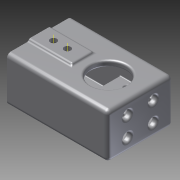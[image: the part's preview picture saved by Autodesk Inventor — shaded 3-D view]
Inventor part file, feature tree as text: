
AUTODESK INVENTOR PART (.ipt)
format: ipt  version: 2012 (Build 160160000, 160)  size: 1,043,968 bytes
history: native  units: mm
features: extrude x30, sketch x30, fillet x15, reference x11, projected_geometry x11, other x4
ambient origin geometry x8: Origin, YZ Plane, XZ Plane, XY Plane, X Axis, Y Axis, Z Axis, Center Point
bodies: Solid1 (feature_tree)
feature tree (101):
  extrude  "Extrusion1"  Depth=2.0mm
  extrude  "Extrusion2"  Depth=2.0mm
  extrude  "Extrusion4"  Depth=3.0mm
  extrude  "Extrusion5"  Depth=3.0mm
  extrude  "Extrusion6"  Depth=0.3mm
  extrude  "Extrusion7"  Depth=0.3mm
  fillet  "Fillet1"  Radius=0.7mm
  extrude  "Extrusion8"  Depth=3.0mm
  extrude  "Extrusion9"  Depth=3.0mm
  extrude  "Extrusion10"  Depth=2.3mm TaperAngle=0.0deg
  extrude  "Extrusion11"  Depth=0.7mm TaperAngle=0.0deg
  other  "Work Axis1"
  extrude  "Extrusion12"  Depth=0.5mm
  extrude  "Extrusion13"  Depth=20.0mm TaperAngle=0.0deg
  extrude  "Extrusion15"  Depth=0.3mm
  other  "Work Axis3"
  extrude  "Extrusion16"  Depth=4.0mm
  extrude  "Extrusion17"  Depth=1.0mm TaperAngle=0.0deg
  extrude  "Extrusion18"  Depth=10.0mm TaperAngle=0.0deg
  extrude  "Extrusion19"  Depth=10.0mm TaperAngle=0.0deg
  extrude  "Extrusion20"  Depth=10.0mm TaperAngle=0.0deg
  fillet  "Fillet3"  Radius=25.903503mm
  fillet  "Fillet4"  Radius=12.951751mm
  fillet  "Fillet5"  Radius=5.0mm
  extrude  "Extrusion21"  Depth=31.903503mm
  extrude  "Extrusion22"  Depth=10.6mm
  extrude  "Extrusion23"  Depth=3.3mm
  extrude  "Extrusion24"  Depth=5.509188mm
  fillet  "Fillet10"  Radius=1.695406mm
  extrude  "Extrusion25"  Depth=1.695406mm
  extrude  "Extrusion26"  Depth=0.6mm TaperAngle=0.0deg
  extrude  "Extrusion27"  Depth=2.0mm
  fillet  "Fillet12"  Radius=3.333333mm
  fillet  "Fillet13"  Radius=10.0mm
  fillet  "Fillet17"  Radius=20.0mm
  extrude  "Extrusion28"  Depth=1.25mm
  fillet  "Fillet18"  Radius=2.5mm
  extrude  "Extrusion29"  Depth=19.403503mm
  fillet  "Fillet19"  Radius=6.467834mm
  fillet  "Fillet20"  Radius=6.467834mm
  fillet  "Fillet21"  Radius=6.467834mm
  fillet  "Fillet22"  Radius=3.333333mm
  extrude  "Extrusion30"  Depth=7.0mm
  other  "Work Axis4"
  other  "Work Axis5"
  extrude  "Extrusion31"  Depth=10.0mm TaperAngle=0.0deg
  fillet  "Fillet23"  Radius=13.2mm
  extrude  "Extrusion32"  Depth=0.5mm
  fillet  "Fillet25"  Radius=0.4mm
  sketch  "Sketch1"  dims[d0=2.0mm d1=2.0mm]
  reference  "Reference1"
  reference  "Reference3"
  reference  "Reference4"
  sketch  "Sketch2"  dims[d2=2.0mm d3=2.0mm]
  sketch  "Sketch3"  dims[d4=3.0mm d5=3.0mm]
  sketch  "Sketch4"  dims[d6=3.0mm d7=3.0mm]
  reference  "Reference6"
  sketch  "Sketch5"  dims[d8=3.0mm d9=0.0mm d10=0.3mm]
  projected_geometry  "Projected Loop1"
  sketch  "Sketch6"  dims[d11=0.3mm d12=0.3mm d14=0.7mm d15=0.0mm]
  sketch  "Sketch7"  dims[d17=3.0mm d18=3.0mm]
  projected_geometry  "Projected Loop2"
  reference  "Reference7"
  reference  "Reference8"
  reference  "Reference9"
  reference  "Reference10"
  sketch  "Sketch8"  dims[d19=3.0mm d20=3.0mm]
  sketch  "Sketch9"  dims[d23=16.0mm d24=0.0mm d26=2.3mm d27=0.0mm]
  reference  "Reference12"
  reference  "Reference13"
  sketch  "Sketch10"  dims[d28=2.0mm d29=0.0mm d30=0.7mm d31=0.0mm]
  reference  "Reference14"
  projected_geometry  "Projected Loop3"
  sketch  "Sketch11"  dims[d32=2.0mm d33=0.5mm]
  sketch  "Sketch12"  dims[d34=0.5mm d35=20.0mm d36=0.0mm]
  sketch  "Sketch15"  dims[d38=1.0mm d39=0.0mm d40=0.3mm]
  sketch  "Sketch16"  dims[d41=1.0mm d42=0.0mm d44=4.0mm]
  sketch  "Sketch17"  dims[d45=4.0mm d46=1.0mm d47=0.0mm]
  sketch  "Sketch18"  dims[d48=10.9mm d49=10.0mm d50=0.0mm]
  sketch  "Sketch19"  dims[d51=1.5mm d52=10.0mm d53=0.0mm]
  sketch  "Sketch20"  dims[d57=12.8mm d58=10.0mm d59=0.0mm d60=25.903503mm d61=12.951751mm d62=5.0mm]
  sketch  "Sketch21"  dims[d63=5.3mm d64=31.903503mm]
  projected_geometry  "Projected Loop4"
  sketch  "Sketch22"  dims[d66=15.951751mm d67=10.6mm]
  projected_geometry  "Projected Loop5"
  sketch  "Sketch24"  dims[d68=10.9mm d69=3.3mm]
  projected_geometry  "Projected Loop6"
  projected_geometry  "Projected Loop7"
  sketch  "Sketch25"  dims[d70=8.9mm d71=5.509188mm d72=1.695406mm]
  sketch  "Sketch26"  dims[d73=1.695406mm d74=1.695406mm]
  projected_geometry  "Projected Loop8"
  sketch  "Sketch27"  dims[d75=10.0mm d76=0.0mm d77=0.6mm d78=0.0mm]
  projected_geometry  "Projected Loop9"
  sketch  "Sketch28"  dims[d79=2.5mm d80=2.0mm d81=3.333333mm d82=10.0mm d83=20.0mm]
  projected_geometry  "Projected Loop10"
  sketch  "Sketch29"  dims[d84=10.0mm d85=0.0mm d86=1.25mm d88=2.5mm]
  sketch  "Sketch30"  dims[d89=2.5mm d90=19.403503mm d91=6.467834mm d92=6.467834mm d93=6.467834mm d94=3.333333mm]
  projected_geometry  "Projected Loop11"
  sketch  "Sketch31"  dims[d95=3.333333mm d96=7.0mm]
  sketch  "Sketch32"  dims[d97=16.7mm d98=10.0mm d99=0.0mm d100=13.2mm]
  sketch  "Sketch33"  dims[d101=10.0mm d102=0.0mm d104=0.5mm d105=0.4mm d106=0.4mm d107=1.0mm d108=1.0mm d109=1.0mm d110=1.0mm d111=0.0mm d112=1.0mm d113=0.0mm d122=25.103503mm d127=4.25mm d128=4.25mm d129=4.25mm d130=4.25mm d131=4.25mm d132=1.0mm d133=0.0mm d135=12.551751mm d136=4.0mm d138=6.275876mm d139=6.275876mm d140=12.551751mm d141=1.0mm d142=0.0mm d143=1.0mm d145=3.64mm d146=0.0mm d147=1.0mm d148=1.0mm d149=1.0mm d150=0.0mm d151=1.0mm d152=0.0mm d153=1.0mm d154=1.0mm d158=0.5mm d159=1.5mm d160=0.0mm d161=0.5mm d162=1.5mm d163=0.0mm d164=0.5mm d165=0.5mm d166=0.5mm d167=0.5mm d168=3.2mm d169=3.2mm d170=6.832425mm d171=9.435898mm d172=20.497274mm d173=4.717949mm d174=4.717949mm d175=6.832425mm d176=1.5mm d177=0.0mm d178=13.4mm d179=10.0mm d180=0.0mm d181=1.0mm d183=0.2mm d184=10.0mm d185=0.0mm d186=1.0mm]
